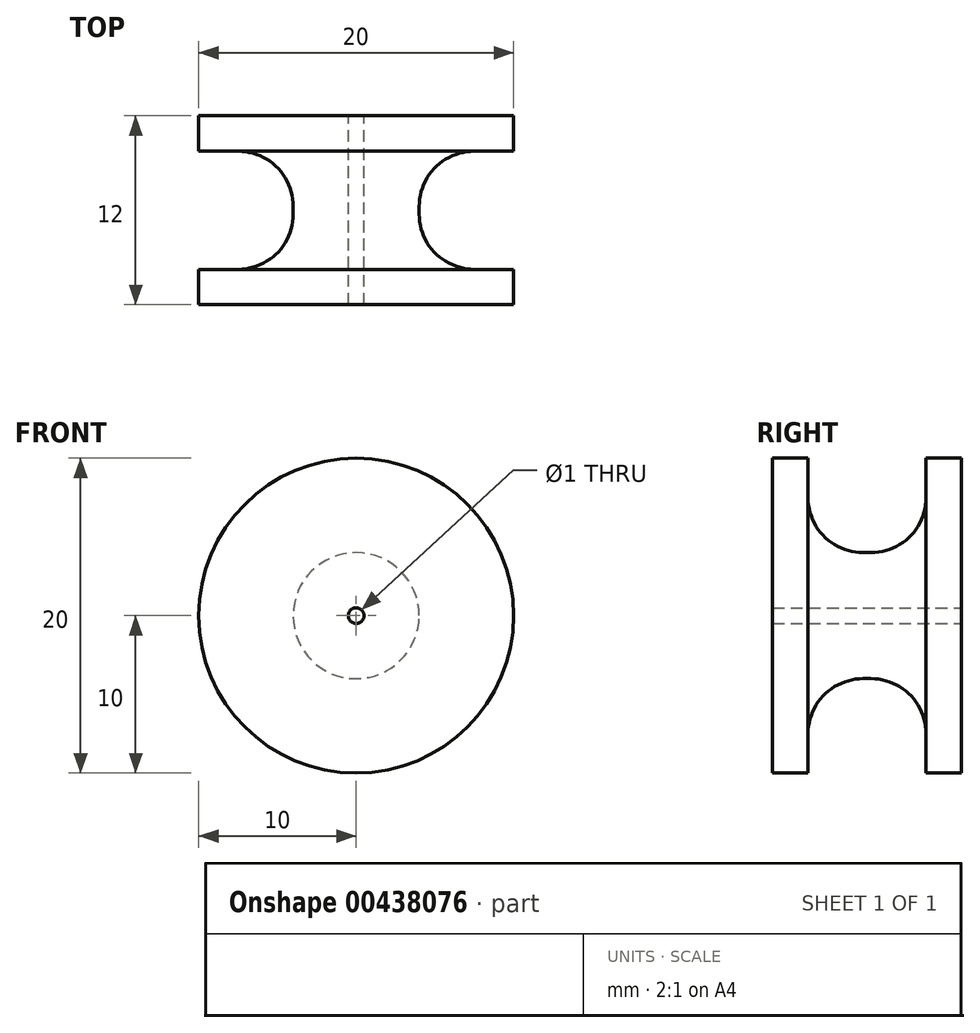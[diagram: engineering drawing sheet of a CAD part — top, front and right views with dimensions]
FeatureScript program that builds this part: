
annotation { "Feature Type Name" : "Feature", "Feature Type Description" : "" }
export const myFeature = defineFeature(function(context is Context, id is Id, definition is map)
    precondition{}
    {
        {
            var Q0;
            Q0=qCreatedBy(makeId("Front.planeOp"),FACE);
            var sketch = newSketch(context, id + "F0", { "sketchPlane" : qUnion([Q0])});
            skCircle(sketch, "E0", {"center": v(0, 0) * mm, "radius": 10 * mm});
            skSolve(sketch);
        }
        {
            var Q0;
            Q0=makeQuery(id+"F0.imprint","IMPRINT",FACE,{"disambiguationData":[TD([[makeQuery(id+"F0.imprint","IMPRINT",EDGE,{"derivedFrom":sQuery(id+"F0.wireOp",EDGE,"E0")}),1.0]])]});
            var Q1;
            Q1=sQuery(id+"F0.wireOp",EDGE,"E0");
            extrude(context, id + "F1", {"entities" : qUnion([Q0]), "surfaceEntities" : qUnion([Q1]), "endBound" : BoundingType.SYMMETRIC, "depth" : 12 * mm});
        }
        {
            var Q0;
            Q0=qCreatedBy(makeId("Top.planeOp"),FACE);
            var sketch = newSketch(context, id + "F2", { "sketchPlane" : qUnion([Q0])});
            skLineSegment(sketch, "E1", {"start": v(0, 41) * mm, "end": v(0, -41.3) * mm});
            skSolve(sketch);
        }
        {
            var Q0;
            Q0=qCreatedBy(makeId("Right.planeOp"),FACE);
            var sketch = newSketch(context, id + "F3", { "sketchPlane" : qUnion([Q0])});
            skLineSegment(sketch, "E2.bottom", {"start": v(-3.75, 10) * mm, "end": v(3.75, 10) * mm});
            skLineSegment(sketch, "E2.top", {"start": v(-0.25, 4) * mm, "end": v(0.25, 4) * mm});
            skLineSegment(sketch, "E2.left", {"start": v(-3.75, 10) * mm, "end": v(-3.75, 7.5) * mm});
            skLineSegment(sketch, "E2.right", {"start": v(3.75, 10) * mm, "end": v(3.75, 7.5) * mm});
            skPoint(sketch, "E3.visualSharp", {"position": v(-3.75, 4) * mm});
            skArc(sketch, "E3.filletArc", {"start": v(-3.75, 7.5) * mm, "mid": v(-2.72, 5.03) * mm, "end": v(-0.25, 4) * mm});
            skPoint(sketch, "E4.visualSharp", {"position": v(3.75, 4) * mm});
            skArc(sketch, "E4.filletArc", {"start": v(0.25, 4) * mm, "mid": v(2.72, 5.03) * mm, "end": v(3.75, 7.5) * mm});
            skSolve(sketch);
        }
        {
            var Q0;
            Q0 = qSketchRegion(id + "F3", true);
            var Q1;
            Q1=sQuery(id+"F2.wireOp",EDGE,"E1");
            revolve(context, id + "F4", {"operationType" : NewBodyOperationType.REMOVE, "entities" : qUnion([Q0]), "axis" : qUnion([Q1]), "revolveType" : RevolveType.FULL, "oppositeDirection" : true});
        }
        {
            var Q0;
            Q0=makeQuery(id+"F1.opExtrude","CAP_FACE",FACE,{"disambiguationData":[OSD([sQuery(id+"F0.wireOp",EDGE,"E0")])],"isStart":true});
            var sketch = newSketch(context, id + "F5", { "sketchPlane" : qUnion([Q0])});
            skCircle(sketch, "E5", {"center": v(0, 0) * mm, "radius": 0.5 * mm});
            skSolve(sketch);
        }
        {
            var Q0;
            Q0=makeQuery(id+"F5.imprint","IMPRINT",FACE,{"disambiguationData":[TD([[makeQuery(id+"F5.imprint","IMPRINT",EDGE,{"derivedFrom":sQuery(id+"F5.wireOp",EDGE,"E5")}),1.0]])]});
            var Q1;
            Q1=sQuery(id+"F5.wireOp",EDGE,"E5");
            extrude(context, id + "F6", {"entities" : qUnion([Q0]), "operationType" : NewBodyOperationType.REMOVE, "surfaceEntities" : qUnion([Q1]), "endBound" : BoundingType.THROUGH_ALL, "oppositeDirection" : true, "depth" : 25 * mm});
        }
    });
